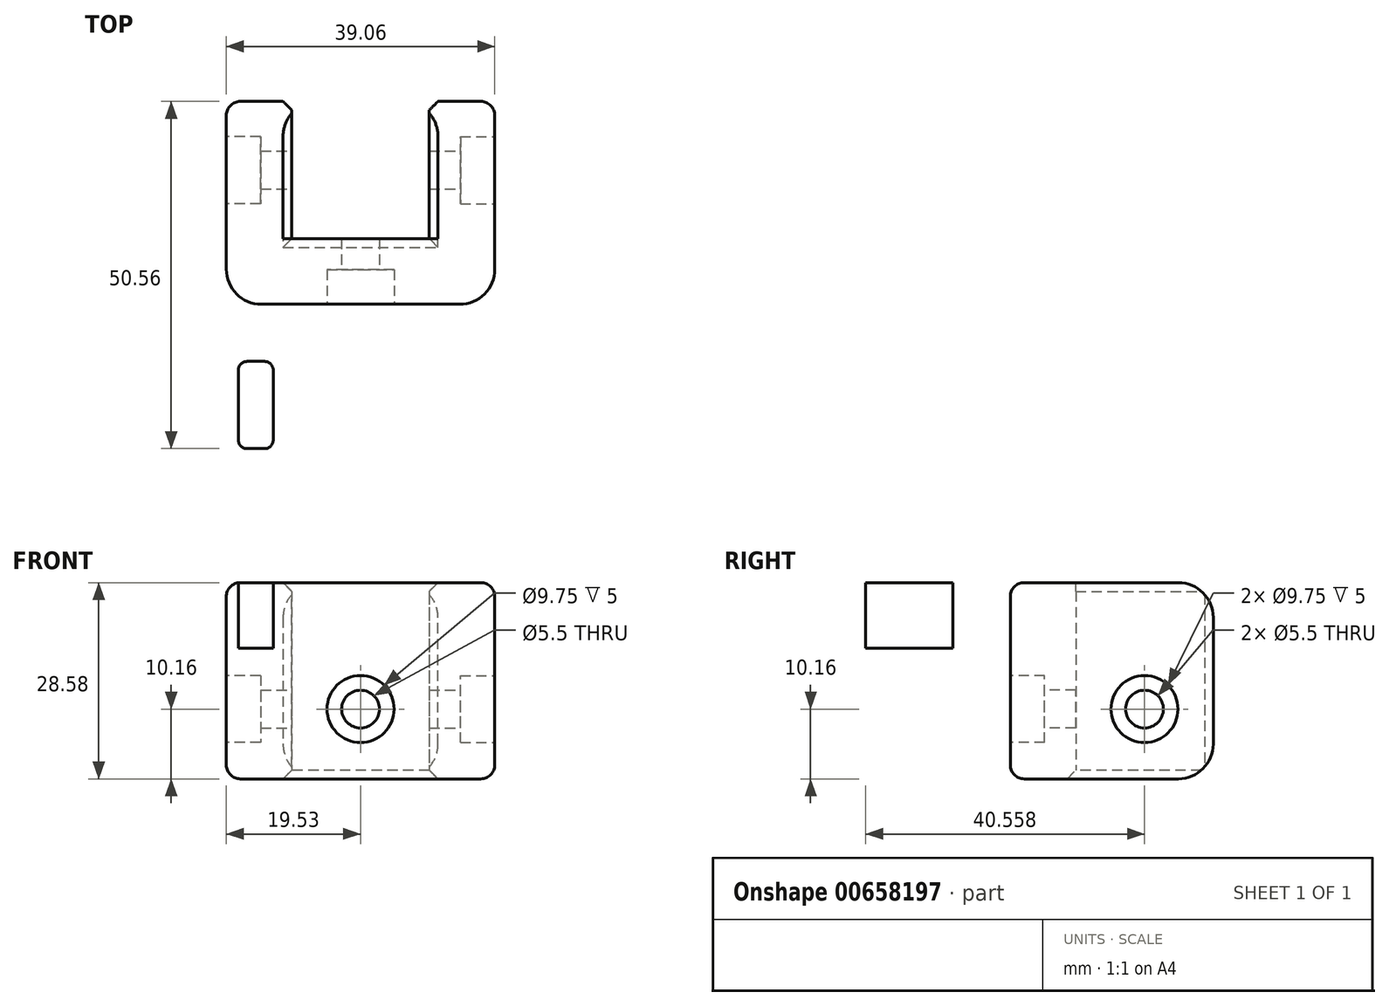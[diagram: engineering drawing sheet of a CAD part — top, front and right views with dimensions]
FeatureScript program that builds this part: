
annotation { "Feature Type Name" : "Feature", "Feature Type Description" : "" }
export const myFeature = defineFeature(function(context is Context, id is Id, definition is map)
    precondition{}
    {
        {
            var Q0;
            Q0=qCreatedBy(makeId("Top.planeOp"),FACE);
            var sketch = newSketch(context, id + "F0", { "sketchPlane" : qUnion([Q0])});
            skPoint(sketch, "E0.middle", {"position": v(0, 0) * mm});
            skArc(sketch, "E1", {"start": v(-25.4, 29.29) * mm, "mid": v(-33.3, 25.07) * mm, "end": v(-34.21, 16.15) * mm});
            skArc(sketch, "E2.MirrorC", {"start": v(25.4, 29.29) * mm, "mid": v(33.3, 25.07) * mm, "end": v(34.21, 16.15) * mm});
            skArc(sketch, "E3", {"start": v(-8.81, -45.85) * mm, "mid": v(0, -51.76) * mm, "end": v(8.81, -45.85) * mm});
            skLineSegment(sketch, "E4", {"start": v(-34.21, 16.15) * mm, "end": v(-8.81, -45.85) * mm});
            skLineSegment(sketch, "E5", {"start": v(34.21, 16.15) * mm, "end": v(8.81, -45.85) * mm});
            skLineSegment(sketch, "E6", {"start": v(-25.4, 29.29) * mm, "end": v(25.4, 29.29) * mm});
            skPoint(sketch, "E7.middle", {"position": v(0, 35.64) * mm});
            skSolve(sketch);
        }
        {
            var Q0;
            Q0=makeQuery(id+"F0.imprint","IMPRINT",FACE,{"disambiguationData":[TD([[makeQuery(id+"F0.imprint","IMPRINT",EDGE,{"derivedFrom":sQuery(id+"F0.wireOp",EDGE,"E1")}),1.0]])]});
            extrude(context, id + "F1", {"entities" : qUnion([Q0]), "depth" : 9.52 * mm, "offsetDistance" : 25.4 * mm});
        }
        {
            var Q0;
            Q0=sQuery(id+"F0.wireOp",VERTEX,"E2.MirrorC.center");
            var Q1;
            Q1=sQuery(id+"F0.wireOp",VERTEX,"E1.center");
            var Q2;
            Q2=sQuery(id+"F0.wireOp",VERTEX,"E3.center");
            var Q3;
            Q3=makeQuery(id+"F1.opExtrude","SWEPT_BODY",BODY,{"disambiguationData":[OSD([sQuery(id+"F0.wireOp",EDGE,"E1"),sQuery(id+"F0.wireOp",EDGE,"E2.MirrorC"),sQuery(id+"F0.wireOp",EDGE,"E3"),sQuery(id+"F0.wireOp",EDGE,"E4"),sQuery(id+"F0.wireOp",EDGE,"E5"),sQuery(id+"F0.wireOp",EDGE,"E6")])]});
            hole(context, id + "F2", {"style" : HoleStyle.C_BORE, "endStyle" : HoleEndStyle.THROUGH, "oppositeDirection" : true, "holeDiameter" : 7.12 * mm, "cBoreDiameter" : 9.75 * mm, "cBoreDepth" : 5 * mm, "majorDiameter" : 6.35 * mm, "isTappedThrough" : true, "tappedDepth" : 12.7 * mm, "tapClearance" : 3, "locations" : qUnion([Q0, Q1, Q2]), "scope" : qUnion([Q3])});
        }
        {
            var Q0;
            Q0=makeQuery(id+"F0.imprint","IMPRINT",FACE,{"disambiguationData":[TD([[makeQuery(id+"F0.imprint","IMPRINT",EDGE,{"derivedFrom":sQuery(id+"F0.wireOp",EDGE,"E1")}),1.0]])]});
            var sketch = newSketch(context, id + "F3", { "sketchPlane" : qUnion([Q0])});
            skLineSegment(sketch, "E8.0", {"start": v(17.78, 5.16) * mm, "end": v(17.78, -5) * mm});
            skLineSegment(sketch, "E9", {"start": v(13.97, -6.27) * mm, "end": v(16.51, -6.27) * mm});
            skLineSegment(sketch, "E10", {"start": v(12.7, -5) * mm, "end": v(12.7, 5.16) * mm});
            skLineSegment(sketch, "E11", {"start": v(13.97, 6.43) * mm, "end": v(16.51, 6.43) * mm});
            skPoint(sketch, "E12.visualSharp", {"position": v(12.7, -6.27) * mm});
            skArc(sketch, "E12.filletArc", {"start": v(12.7, -5) * mm, "mid": v(13.07, -5.9) * mm, "end": v(13.97, -6.27) * mm});
            skPoint(sketch, "E13.visualSharp", {"position": v(17.78, -6.27) * mm});
            skArc(sketch, "E13.filletArc", {"start": v(16.51, -6.27) * mm, "mid": v(17.4, -5.9) * mm, "end": v(17.78, -5) * mm});
            skPoint(sketch, "E14.visualSharp", {"position": v(17.78, 6.43) * mm});
            skArc(sketch, "E14.filletArc", {"start": v(17.78, 5.16) * mm, "mid": v(17.4, 6.06) * mm, "end": v(16.51, 6.43) * mm});
            skPoint(sketch, "E15.visualSharp", {"position": v(12.7, 6.43) * mm});
            skArc(sketch, "E15.filletArc", {"start": v(13.97, 6.43) * mm, "mid": v(13.07, 6.06) * mm, "end": v(12.7, 5.16) * mm});
            skArc(sketch, "E16.MirrorCS", {"start": v(-13.97, 6.43) * mm, "mid": v(-13.07, 6.06) * mm, "end": v(-12.7, 5.16) * mm});
            skArc(sketch, "E17.MirrorCS", {"start": v(-16.51, -6.27) * mm, "mid": v(-17.4, -5.9) * mm, "end": v(-17.78, -5) * mm});
            skArc(sketch, "E18.MirrorCS", {"start": v(-12.7, -5) * mm, "mid": v(-13.07, -5.9) * mm, "end": v(-13.97, -6.27) * mm});
            skArc(sketch, "E19.MirrorCS", {"start": v(-17.78, 5.16) * mm, "mid": v(-17.4, 6.06) * mm, "end": v(-16.51, 6.43) * mm});
            skPoint(sketch, "E20.MirrorP", {"position": v(-17.78, -6.27) * mm});
            skPoint(sketch, "E21.MirrorP", {"position": v(-12.7, -6.27) * mm});
            skLineSegment(sketch, "E22.MirrorCS", {"start": v(-17.78, 5.16) * mm, "end": v(-17.78, -5) * mm});
            skLineSegment(sketch, "E23.MirrorCS", {"start": v(-13.97, -6.27) * mm, "end": v(-16.51, -6.27) * mm});
            skPoint(sketch, "E24.MirrorP", {"position": v(-12.7, 6.43) * mm});
            skPoint(sketch, "E25.MirrorP", {"position": v(-17.78, 6.43) * mm});
            skLineSegment(sketch, "E26.MirrorCS", {"start": v(-13.97, 6.43) * mm, "end": v(-16.51, 6.43) * mm});
            skLineSegment(sketch, "E27.MirrorCS", {"start": v(-12.7, -5) * mm, "end": v(-12.7, 5.16) * mm});
            skLineSegment(sketch, "E28.bottom", {"start": v(10, 24.29) * mm, "end": v(-10, 24.29) * mm});
            skLineSegment(sketch, "E28.top", {"start": v(10, 14.76) * mm, "end": v(-10, 14.76) * mm});
            skLineSegment(sketch, "E28.left", {"start": v(10, 24.29) * mm, "end": v(10, 14.76) * mm});
            skLineSegment(sketch, "E28.right", {"start": v(-10, 24.29) * mm, "end": v(-10, 14.76) * mm});
            skPoint(sketch, "E28.middle", {"position": v(0, 19.53) * mm});
            skLineSegment(sketch, "E29.bottom", {"start": v(10, 24.29) * mm, "end": v(19.53, 24.29) * mm});
            skLineSegment(sketch, "E29.top", {"start": v(10, 44.29) * mm, "end": v(19.52, 44.29) * mm});
            skLineSegment(sketch, "E29.left", {"start": v(10, 24.29) * mm, "end": v(10, 44.29) * mm});
            skLineSegment(sketch, "E29.right", {"start": v(19.53, 24.29) * mm, "end": v(19.52, 44.29) * mm});
            skLineSegment(sketch, "E30.MirrorCS", {"start": v(-10, 24.29) * mm, "end": v(-10, 44.29) * mm});
            skLineSegment(sketch, "E31.MirrorCS", {"start": v(-10, 44.29) * mm, "end": v(-19.52, 44.29) * mm});
            skLineSegment(sketch, "E32.MirrorCS", {"start": v(-19.53, 24.29) * mm, "end": v(-19.53, 44.29) * mm});
            skLineSegment(sketch, "E33.MirrorCS", {"start": v(-10, 24.29) * mm, "end": v(-19.53, 24.29) * mm});
            skLineSegment(sketch, "E34.top", {"start": v(-10, 14.76) * mm, "end": v(-19.53, 14.76) * mm});
            skLineSegment(sketch, "E34.right", {"start": v(-19.53, 24.29) * mm, "end": v(-19.53, 14.76) * mm});
            skLineSegment(sketch, "E35.MirrorCS", {"start": v(10, 14.76) * mm, "end": v(19.53, 14.76) * mm});
            skLineSegment(sketch, "E36.MirrorCS", {"start": v(19.53, 24.29) * mm, "end": v(19.53, 14.76) * mm});
            skSolve(sketch);
        }
        {
            var Q0;
            Q0=makeQuery(id+"F3.imprint","IMPRINT",FACE,{"disambiguationData":[TD([[makeQuery(id+"F3.imprint","IMPRINT",EDGE,{"derivedFrom":sQuery(id+"F3.wireOp",EDGE,"E8.0")}),-1.0]])]});
            var Q1;
            Q1=makeQuery(id+"F3.imprint","IMPRINT",FACE,{"disambiguationData":[TD([[makeQuery(id+"F3.imprint","IMPRINT",EDGE,{"derivedFrom":sQuery(id+"F3.wireOp",EDGE,"E16.MirrorCS")}),-1.0]])]});
            var Q2;
            Q2=makeQuery(id+"F3.imprint","IMPRINT",FACE,{"disambiguationData":[TD([[makeQuery(id+"F3.imprint","IMPRINT",EDGE,{"derivedFrom":sQuery(id+"F3.wireOp",EDGE,"Prlfpxv0-Jh6N-6gBG-48OY-dPIFZnCftuaz.bottom")}),-1.0]])]});
            extrude(context, id + "F4", {"entities" : qUnion([Q0, Q1, Q2]), "operationType" : NewBodyOperationType.REMOVE, "endBound" : BoundingType.UP_TO_NEXT, "depth" : 25.4 * mm, "offsetDistance" : 25.4 * mm});
        }
        {
            var Q0;
            {var subQ0=sQuery(id+"F3.wireOp",EDGE,"E28.bottom");Q0=makeQuery(id+"F3.imprint","IMPRINT",FACE,{"disambiguationData":[TD([[makeQuery(id+"F3.imprint","IMPRINT",EDGE,{"derivedFrom":subQ0}),-1.0]])]});}
            var Q1;
            Q1=makeQuery(id+"F1.opExtrude","CAP_FACE",FACE,{"disambiguationData":[OSD([sQuery(id+"F0.wireOp",EDGE,"E1"),sQuery(id+"F0.wireOp",EDGE,"E2.MirrorC"),sQuery(id+"F0.wireOp",EDGE,"E3"),sQuery(id+"F0.wireOp",EDGE,"E4"),sQuery(id+"F0.wireOp",EDGE,"E5"),sQuery(id+"F0.wireOp",EDGE,"E6")])],"isStart":false});
            extrude(context, id + "F5", {"entities" : qUnion([Q0]), "operationType" : NewBodyOperationType.REMOVE, "endBound" : BoundingType.UP_TO_SURFACE, "depth" : 25.4 * mm, "endBoundEntityFace" : qUnion([Q1]), "offsetDistance" : 25.4 * mm});
        }
        {
            var Q0;
            {var subQ0=sQuery(id+"F3.wireOp",EDGE,"E31.MirrorCS");Q0=makeQuery(id+"F3.imprint","IMPRINT",FACE,{"disambiguationData":[TD([[makeQuery(id+"F3.imprint","IMPRINT",EDGE,{"derivedFrom":subQ0}),1.0]])]});}
            var Q1;
            {var subQ0=sQuery(id+"F3.wireOp",EDGE,"E29.top");Q1=makeQuery(id+"F3.imprint","IMPRINT",FACE,{"disambiguationData":[TD([[makeQuery(id+"F3.imprint","IMPRINT",EDGE,{"derivedFrom":subQ0}),-1.0]])]});}
            extrude(context, id + "F6", {"entities" : qUnion([Q0, Q1]), "operationType" : NewBodyOperationType.ADD, "depth" : 9.52 * mm, "offsetDistance" : 25.4 * mm});
        }
        {
            var Q0;
            {var subQ0=sQuery(id+"F3.wireOp",EDGE,"E29.top");Q0=makeQuery(id+"F3.imprint","IMPRINT",FACE,{"disambiguationData":[TD([[makeQuery(id+"F3.imprint","IMPRINT",EDGE,{"derivedFrom":subQ0}),-1.0]])]});}
            var Q1;
            {var subQ0=sQuery(id+"F3.wireOp",EDGE,"E29.bottom");Q1=makeQuery(id+"F3.imprint","IMPRINT",FACE,{"disambiguationData":[TD([[makeQuery(id+"F3.imprint","IMPRINT",EDGE,{"derivedFrom":subQ0}),1.0]])]});}
            var Q2;
            Q2=makeQuery(id+"F3.imprint","IMPRINT",FACE,{"disambiguationData":[TD([[makeQuery(id+"F3.imprint","IMPRINT",EDGE,{"derivedFrom":sQuery(id+"F3.wireOp",EDGE,"E28.left")}),1.0]])]});
            var Q3;
            Q3=makeQuery(id+"F3.imprint","IMPRINT",FACE,{"disambiguationData":[TD([[makeQuery(id+"F3.imprint","IMPRINT",EDGE,{"derivedFrom":sQuery(id+"F3.wireOp",EDGE,"E28.bottom")}),1.0]])]});
            var Q4;
            Q4=makeQuery(id+"F3.imprint","IMPRINT",FACE,{"disambiguationData":[TD([[makeQuery(id+"F3.imprint","IMPRINT",EDGE,{"derivedFrom":sQuery(id+"F3.wireOp",EDGE,"E33.MirrorCS")}),1.0]])]});
            var Q5;
            {var subQ0=sQuery(id+"F3.wireOp",EDGE,"E33.MirrorCS");Q5=makeQuery(id+"F3.imprint","IMPRINT",FACE,{"disambiguationData":[TD([[makeQuery(id+"F3.imprint","IMPRINT",EDGE,{"derivedFrom":subQ0}),-1.0]])]});}
            var Q6;
            {var subQ0=sQuery(id+"F3.wireOp",EDGE,"E31.MirrorCS");Q6=makeQuery(id+"F3.imprint","IMPRINT",FACE,{"disambiguationData":[TD([[makeQuery(id+"F3.imprint","IMPRINT",EDGE,{"derivedFrom":subQ0}),1.0]])]});}
            extrude(context, id + "F7", {"entities" : qUnion([Q0, Q1, Q2, Q3, Q4, Q5, Q6]), "operationType" : NewBodyOperationType.ADD, "oppositeDirection" : true, "depth" : 19.05 * mm, "offsetDistance" : 25.4 * mm});
        }
        {
            var Q0;
            {var subQ0=sQuery(id+"F3.wireOp",EDGE,"E31.MirrorCS");var subQ1=sQuery(id+"F3.wireOp",EDGE,"E30.MirrorCS");Q0=makeQuery(id+"F7.boolean.opBoolean","MERGE",EDGE,{"derivedFrom":[makeQuery(id+"F6.opExtrude","SWEPT_EDGE",EDGE,{"disambiguationData":[OSD([subQ1,subQ0])]}),makeQuery(id+"F7.opExtrude","SWEPT_EDGE",EDGE,{"disambiguationData":[OSD([subQ1,subQ0])]})]});}
            var Q1;
            Q1=makeQuery(id+"F7.opExtrude","CAP_EDGE",EDGE,{"disambiguationData":[OSD([sQuery(id+"F3.wireOp",EDGE,"E30.MirrorCS")])],"isStart":false});
            var Q2;
            Q2=makeQuery(id+"F7.opExtrude","CAP_EDGE",EDGE,{"disambiguationData":[OSD([sQuery(id+"F3.wireOp",EDGE,"E28.bottom")])],"isStart":false});
            var Q3;
            Q3=makeQuery(id+"F7.opExtrude","CAP_EDGE",EDGE,{"disambiguationData":[OSD([sQuery(id+"F3.wireOp",EDGE,"E29.left")])],"isStart":false});
            var Q4;
            {var subQ0=sQuery(id+"F3.wireOp",EDGE,"E29.left");var subQ1=sQuery(id+"F3.wireOp",EDGE,"E29.top");Q4=makeQuery(id+"F7.boolean.opBoolean","MERGE",EDGE,{"derivedFrom":[makeQuery(id+"F6.opExtrude","SWEPT_EDGE",EDGE,{"disambiguationData":[OSD([subQ1,subQ0])]}),makeQuery(id+"F7.opExtrude","SWEPT_EDGE",EDGE,{"disambiguationData":[OSD([subQ1,subQ0])]})]});}
            var Q5;
            {var subQ0=sQuery(id+"F3.wireOp",EDGE,"E29.left");var subQ1=sQuery(id+"F0.wireOp",EDGE,"E6");Q5=makeQuery(id+"F6.boolean.opBoolean","MERGE",EDGE,{"derivedFrom":[makeQuery(id+"F5.boolean.opBoolean","COPY",EDGE,{"derivedFrom":makeQuery(id+"F5.opExtrude","TWEAK_EDGE",EDGE,{"derivedFrom":[makeQuery(id+"F3.imprint","IMPRINT",EDGE,{"disambiguationData":[TD([[makeQuery(id+"F3.imprint","INTERSECT",VERTEX,{"derivedFrom":[makeQuery(id+"F0.imprint","IMPRINT",EDGE,{"derivedFrom":subQ1}),subQ0]}),1.0]])],"derivedFrom":subQ0}),makeQuery(id+"F1.opExtrude","CAP_FACE",FACE,{"disambiguationData":[OSD([sQuery(id+"F0.wireOp",EDGE,"E1"),sQuery(id+"F0.wireOp",EDGE,"E2.MirrorC"),sQuery(id+"F0.wireOp",EDGE,"E3"),sQuery(id+"F0.wireOp",EDGE,"E4"),sQuery(id+"F0.wireOp",EDGE,"E5"),subQ1])],"isStart":false})]})}),makeQuery(id+"F6.opExtrude","CAP_EDGE",EDGE,{"disambiguationData":[OSD([subQ0])],"isStart":false})]});}
            var Q6;
            {var subQ0=sQuery(id+"F3.wireOp",EDGE,"E30.MirrorCS");var subQ1=sQuery(id+"F0.wireOp",EDGE,"E6");Q6=makeQuery(id+"F6.boolean.opBoolean","MERGE",EDGE,{"derivedFrom":[makeQuery(id+"F5.boolean.opBoolean","COPY",EDGE,{"derivedFrom":makeQuery(id+"F5.opExtrude","TWEAK_EDGE",EDGE,{"derivedFrom":[makeQuery(id+"F3.imprint","IMPRINT",EDGE,{"disambiguationData":[TD([[makeQuery(id+"F3.imprint","INTERSECT",VERTEX,{"derivedFrom":[makeQuery(id+"F0.imprint","IMPRINT",EDGE,{"derivedFrom":subQ1}),subQ0]}),1.0]])],"derivedFrom":subQ0}),makeQuery(id+"F1.opExtrude","CAP_FACE",FACE,{"disambiguationData":[OSD([sQuery(id+"F0.wireOp",EDGE,"E1"),sQuery(id+"F0.wireOp",EDGE,"E2.MirrorC"),sQuery(id+"F0.wireOp",EDGE,"E3"),sQuery(id+"F0.wireOp",EDGE,"E4"),sQuery(id+"F0.wireOp",EDGE,"E5"),subQ1])],"isStart":false})]})}),makeQuery(id+"F6.opExtrude","CAP_EDGE",EDGE,{"disambiguationData":[OSD([subQ0])],"isStart":false})]});}
            var Q7;
            Q7=makeQuery(id+"F5.boolean.opBoolean","COPY",EDGE,{"derivedFrom":makeQuery(id+"F5.opExtrude","TWEAK_EDGE",EDGE,{"derivedFrom":[makeQuery(id+"F3.imprint","IMPRINT",EDGE,{"derivedFrom":sQuery(id+"F3.wireOp",EDGE,"E28.bottom")}),makeQuery(id+"F1.opExtrude","CAP_FACE",FACE,{"disambiguationData":[OSD([sQuery(id+"F0.wireOp",EDGE,"E1"),sQuery(id+"F0.wireOp",EDGE,"E2.MirrorC"),sQuery(id+"F0.wireOp",EDGE,"E3"),sQuery(id+"F0.wireOp",EDGE,"E4"),sQuery(id+"F0.wireOp",EDGE,"E5"),sQuery(id+"F0.wireOp",EDGE,"E6")])],"isStart":false})]})});
            chamfer(context, id + "F8", {"entities" : qUnion([Q0, Q1, Q2, Q3, Q4, Q5, Q6, Q7]), "width" : 1.27 * mm, "tangentPropagation" : true});
        }
        {
            var Q0;
            {var subQ0=sQuery(id+"F3.wireOp",EDGE,"E32.MirrorCS");Q0=makeQuery(id+"F7.boolean.opBoolean","MERGE",FACE,{"derivedFrom":[makeQuery(id+"F6.opExtrude","SWEPT_FACE",FACE,{"disambiguationData":[OSD([subQ0])]}),makeQuery(id+"F7.opExtrude","SWEPT_FACE",FACE,{"disambiguationData":[OSD([subQ0,sQuery(id+"F3.wireOp",EDGE,"E34.right")])]})]});}
            var sketch = newSketch(context, id + "F9", { "sketchPlane" : qUnion([Q0])});
            skPoint(sketch, "E37", {"position": v(-34.29, -8.89) * mm});
            skPoint(sketch, "E37.positionSnap0", {"position": v(-34.29, -19.05) * mm});
            skSolve(sketch);
        }
        {
            var Q0;
            {var subQ0=sQuery(id+"F3.wireOp",EDGE,"E29.right");Q0=makeQuery(id+"F7.boolean.opBoolean","MERGE",FACE,{"derivedFrom":[makeQuery(id+"F6.opExtrude","SWEPT_FACE",FACE,{"disambiguationData":[OSD([subQ0])]}),makeQuery(id+"F7.opExtrude","SWEPT_FACE",FACE,{"disambiguationData":[OSD([subQ0,sQuery(id+"F3.wireOp",EDGE,"E36.MirrorCS")])]})]});}
            var sketch = newSketch(context, id + "F10", { "sketchPlane" : qUnion([Q0])});
            skPoint(sketch, "E38", {"position": v(34.29, -8.89) * mm});
            skPoint(sketch, "E38.positionSnap0", {"position": v(34.29, -19.05) * mm});
            skSolve(sketch);
        }
        {
            var Q0;
            Q0=makeQuery(id+"F7.opExtrude","SWEPT_FACE",FACE,{"disambiguationData":[OSD([sQuery(id+"F3.wireOp",EDGE,"E28.top"),sQuery(id+"F3.wireOp",EDGE,"E34.top"),sQuery(id+"F3.wireOp",EDGE,"E35.MirrorCS")])]});
            var sketch = newSketch(context, id + "F11", { "sketchPlane" : qUnion([Q0])});
            skPoint(sketch, "E39", {"position": v(0, -8.89) * mm});
            skSolve(sketch);
        }
        {
            var Q0;
            Q0=sQuery(id+"F10.wireOp",VERTEX,"E38");
            var Q1;
            Q1=sQuery(id+"F11.wireOp",VERTEX,"E39");
            var Q2;
            Q2=sQuery(id+"F9.wireOp",VERTEX,"E37");
            var Q3;
            Q3=makeQuery(id+"F1.opExtrude","SWEPT_BODY",BODY,{"disambiguationData":[OSD([sQuery(id+"F0.wireOp",EDGE,"E1"),sQuery(id+"F0.wireOp",EDGE,"E2.MirrorC"),sQuery(id+"F0.wireOp",EDGE,"E3"),sQuery(id+"F0.wireOp",EDGE,"E4"),sQuery(id+"F0.wireOp",EDGE,"E5"),sQuery(id+"F0.wireOp",EDGE,"E6")])]});
            hole(context, id + "F12", {"style" : HoleStyle.C_BORE, "endStyle" : HoleEndStyle.THROUGH, "standardTappedOrClearance" : lookupTablePath({ "standard" : "ISO", "fit" : "Normal", "size" : "M5", "type" : "Clearance" }), "standardBlindInLast" : lookupTablePath({ "fit" : "Standard", "standard" : "ISO", "size" : "M5", "type" : "Clearance" }), "holeDiameter" : 5.5 * mm, "cBoreDiameter" : 9.75 * mm, "cBoreDepth" : 5 * mm, "majorDiameter" : 6.35 * mm, "isTappedThrough" : true, "tappedDepth" : 12.7 * mm, "tapClearance" : 3, "locations" : qUnion([Q0, Q1, Q2]), "scope" : qUnion([Q3])});
        }
        {
            var Q0;
            Q0=makeQuery(id+"F7.opExtrude","SWEPT_EDGE",EDGE,{"disambiguationData":[OSD([sQuery(id+"F3.wireOp",EDGE,"E35.MirrorCS"),sQuery(id+"F3.wireOp",EDGE,"E36.MirrorCS")])]});
            var Q1;
            Q1=makeQuery(id+"F7.opExtrude","SWEPT_EDGE",EDGE,{"disambiguationData":[OSD([sQuery(id+"F3.wireOp",EDGE,"E34.top"),sQuery(id+"F3.wireOp",EDGE,"E34.right")])]});
            var Q2;
            Q2=makeQuery(id+"F7.opExtrude","CAP_EDGE",EDGE,{"disambiguationData":[OSD([sQuery(id+"F3.wireOp",EDGE,"E31.MirrorCS")])],"isStart":false});
            var Q3;
            Q3=makeQuery(id+"F7.opExtrude","CAP_EDGE",EDGE,{"disambiguationData":[OSD([sQuery(id+"F3.wireOp",EDGE,"E29.top")])],"isStart":false});
            var Q4;
            Q4=makeQuery(id+"F6.opExtrude","CAP_EDGE",EDGE,{"disambiguationData":[OSD([sQuery(id+"F3.wireOp",EDGE,"E31.MirrorCS")])],"isStart":false});
            var Q5;
            Q5=makeQuery(id+"F6.opExtrude","CAP_EDGE",EDGE,{"disambiguationData":[OSD([sQuery(id+"F3.wireOp",EDGE,"E29.top")])],"isStart":false});
            fillet(context, id + "F13", {"entities" : qUnion([Q0, Q1, Q2, Q3, Q4, Q5]), "radius" : 5.08 * mm, "tangentPropagation" : true, "allowEdgeOverflow" : false});
        }
        {
            var Q0;
            Q0=makeQuery(id+"F7.opExtrude","CAP_EDGE",EDGE,{"disambiguationData":[OSD([sQuery(id+"F3.wireOp",EDGE,"E29.right"),sQuery(id+"F3.wireOp",EDGE,"E36.MirrorCS")])],"isStart":false});
            var Q1;
            Q1=makeQuery(id+"F1.opExtrude","CAP_EDGE",EDGE,{"disambiguationData":[OSD([sQuery(id+"F0.wireOp",EDGE,"E5")])],"isStart":true});
            var Q2;
            Q2=makeQuery(id+"F1.opExtrude","CAP_EDGE",EDGE,{"disambiguationData":[OSD([sQuery(id+"F0.wireOp",EDGE,"E2.MirrorC")])],"isStart":false});
            var Q3;
            Q3=makeQuery(id+"F7.opExtrude","CAP_EDGE",EDGE,{"disambiguationData":[OSD([sQuery(id+"F3.wireOp",EDGE,"E28.top"),sQuery(id+"F3.wireOp",EDGE,"E34.top"),sQuery(id+"F3.wireOp",EDGE,"E35.MirrorCS")])],"isStart":true});
            fillet(context, id + "F14", {"entities" : qUnion([Q0, Q1, Q2, Q3]), "radius" : 2.03 * mm, "tangentPropagation" : true, "allowEdgeOverflow" : false});
        }
    });
